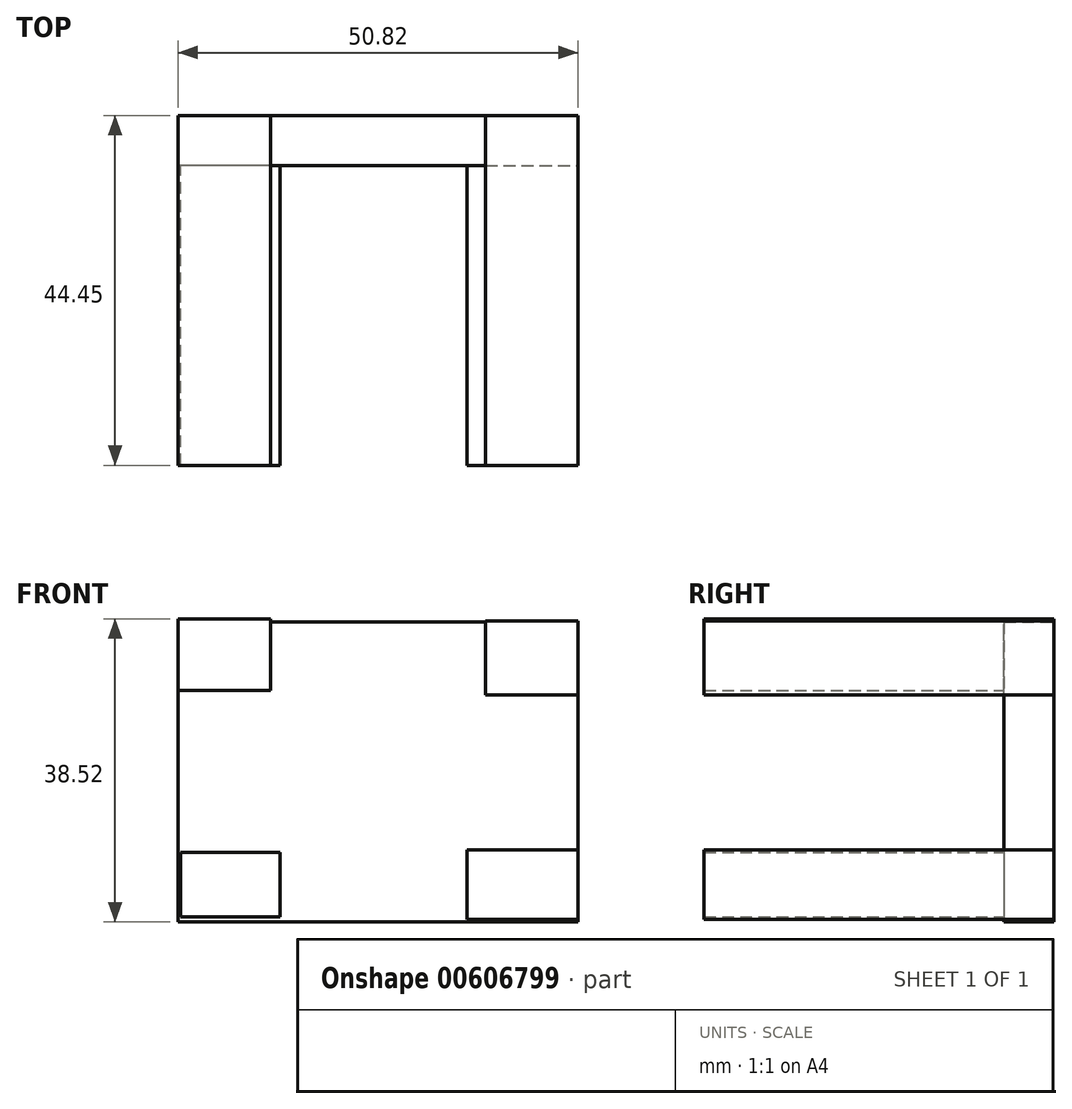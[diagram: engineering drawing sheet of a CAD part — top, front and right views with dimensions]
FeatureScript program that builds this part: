
annotation { "Feature Type Name" : "Feature", "Feature Type Description" : "" }
export const myFeature = defineFeature(function(context is Context, id is Id, definition is map)
    precondition{}
    {
        {
            var Q0;
            Q0=qCreatedBy(makeId("Front.planeOp"),FACE);
            var sketch = newSketch(context, id + "F0", { "sketchPlane" : qUnion([Q0])});
            skLineSegment(sketch, "E0.bottom", {"start": v(-21.3, 22.48) * mm, "end": v(29.5, 22.48) * mm});
            skLineSegment(sketch, "E0.top", {"start": v(-21.3, -15.62) * mm, "end": v(29.5, -15.62) * mm});
            skLineSegment(sketch, "E0.left", {"start": v(-21.3, 22.48) * mm, "end": v(-21.3, -15.62) * mm});
            skLineSegment(sketch, "E0.right", {"start": v(29.5, 22.48) * mm, "end": v(29.5, -15.62) * mm});
            skSolve(sketch);
        }
        {
            var Q0;
            Q0 = qSketchRegion(id + "F0", true);
            extrude(context, id + "F1", {"entities" : qUnion([Q0]), "depth" : 6.35 * mm, "offsetDistance" : 25.4 * mm});
        }
        {
            var Q0;
            Q0=qCreatedBy(makeId("Front.planeOp"),FACE);
            var sketch = newSketch(context, id + "F2", { "sketchPlane" : qUnion([Q0])});
            skLineSegment(sketch, "E1.bottom", {"start": v(-21.29, 22.9) * mm, "end": v(-9.54, 22.9) * mm});
            skLineSegment(sketch, "E1.top", {"start": v(-21.29, 13.8) * mm, "end": v(-9.54, 13.8) * mm});
            skLineSegment(sketch, "E1.left", {"start": v(-21.29, 22.9) * mm, "end": v(-21.29, 13.8) * mm});
            skLineSegment(sketch, "E1.right", {"start": v(-9.54, 22.9) * mm, "end": v(-9.54, 13.8) * mm});
            skLineSegment(sketch, "E2.bottom", {"start": v(-21, -14.97) * mm, "end": v(-8.37, -14.97) * mm});
            skLineSegment(sketch, "E2.top", {"start": v(-21, -6.75) * mm, "end": v(-8.37, -6.75) * mm});
            skLineSegment(sketch, "E2.left", {"start": v(-21, -14.97) * mm, "end": v(-21, -6.75) * mm});
            skLineSegment(sketch, "E2.right", {"start": v(-8.37, -14.97) * mm, "end": v(-8.37, -6.75) * mm});
            skLineSegment(sketch, "E3.bottom", {"start": v(29.5, 22.6) * mm, "end": v(17.76, 22.6) * mm});
            skLineSegment(sketch, "E3.top", {"start": v(29.5, 13.21) * mm, "end": v(17.76, 13.21) * mm});
            skLineSegment(sketch, "E3.left", {"start": v(29.5, 22.6) * mm, "end": v(29.5, 13.21) * mm});
            skLineSegment(sketch, "E3.right", {"start": v(17.76, 22.6) * mm, "end": v(17.76, 13.21) * mm});
            skLineSegment(sketch, "E4.bottom", {"start": v(29.5, -15.27) * mm, "end": v(15.41, -15.27) * mm});
            skLineSegment(sketch, "E4.top", {"start": v(29.5, -6.46) * mm, "end": v(15.41, -6.46) * mm});
            skLineSegment(sketch, "E4.left", {"start": v(29.5, -15.27) * mm, "end": v(29.5, -6.46) * mm});
            skLineSegment(sketch, "E4.right", {"start": v(15.41, -15.27) * mm, "end": v(15.41, -6.46) * mm});
            skSolve(sketch);
        }
        {
            var Q0;
            Q0 = qSketchRegion(id + "F2", true);
            extrude(context, id + "F3", {"entities" : qUnion([Q0]), "operationType" : NewBodyOperationType.ADD, "depth" : 44.45 * mm, "offsetDistance" : 25.4 * mm});
        }
    });
